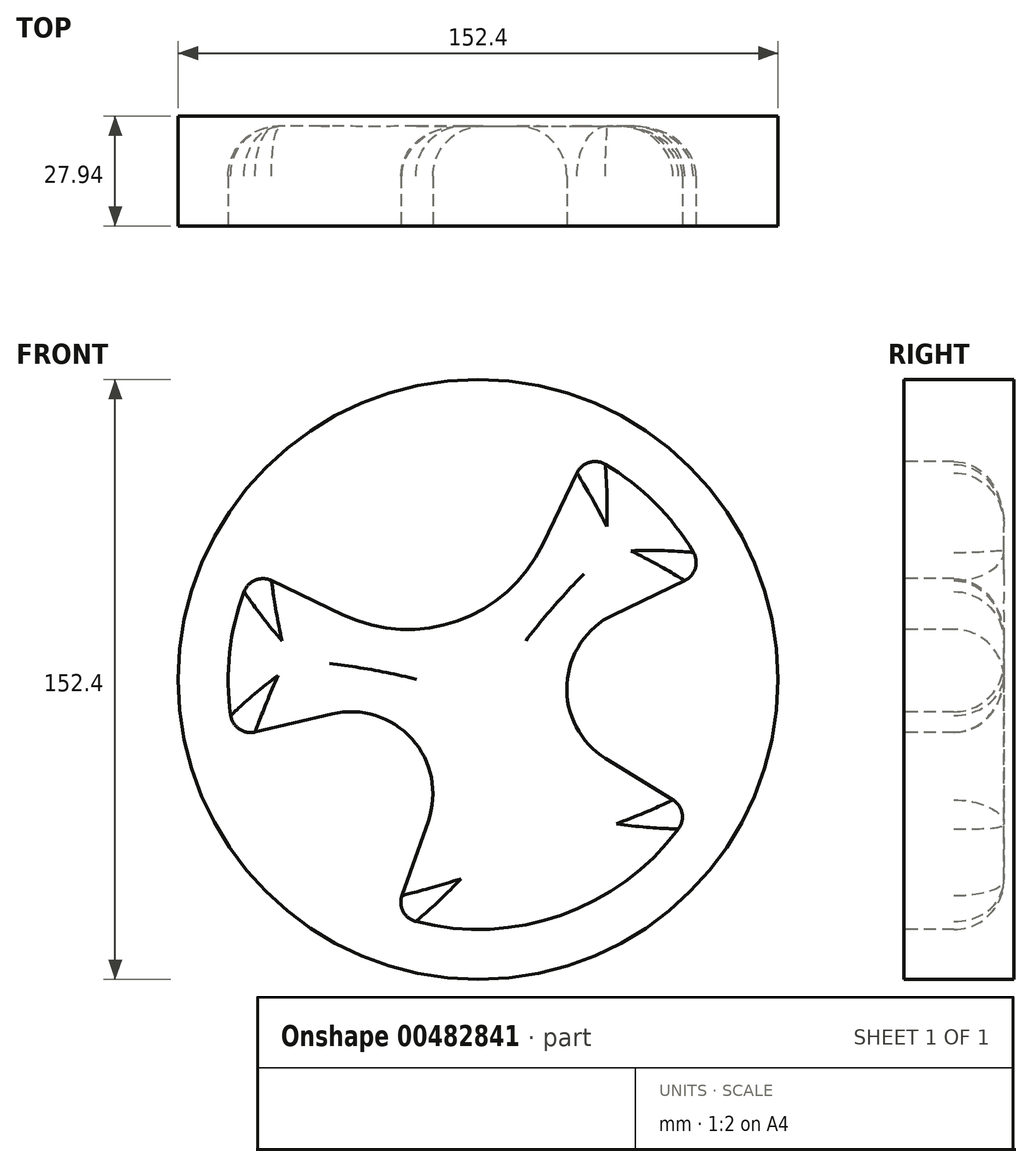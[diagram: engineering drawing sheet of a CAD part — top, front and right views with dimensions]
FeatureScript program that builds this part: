
annotation { "Feature Type Name" : "Feature", "Feature Type Description" : "" }
export const myFeature = defineFeature(function(context is Context, id is Id, definition is map)
    precondition{}
    {
        {
            var Q0;
            Q0=qCreatedBy(makeId("Front.planeOp"),FACE);
            var sketch = newSketch(context, id + "F0", { "sketchPlane" : qUnion([Q0])});
            skCircle(sketch, "E0", {"center": v(0, 0) * mm, "radius": 76.2 * mm});
            skSolve(sketch);
        }
        {
            var Q0;
            Q0=makeQuery(id+"F0.imprint","IMPRINT",FACE,{"disambiguationData":[TD([[makeQuery(id+"F0.imprint","IMPRINT",EDGE,{"derivedFrom":sQuery(id+"F0.wireOp",EDGE,"E0")}),1.0]])]});
            extrude(context, id + "F1", {"entities" : qUnion([Q0]), "depth" : 27.94 * mm});
        }
        {
            var Q0;
            Q0=makeQuery(id+"F1.opExtrude","CAP_FACE",FACE,{"disambiguationData":[OSD([sQuery(id+"F0.wireOp",EDGE,"E0")])],"isStart":false});
            var sketch = newSketch(context, id + "F2", { "sketchPlane" : qUnion([Q0])});
            skPoint(sketch, "E1.center.orphan", {"position": v(0, 50.8) * mm});
            skLineSegment(sketch, "E2.1.0", {"start": v(-34.37, 16.45) * mm, "end": v(-52.5, 25.13) * mm});
            skLineSegment(sketch, "E2.4.2", {"start": v(-12.67, -35.93) * mm, "end": v(-19.35, -54.89) * mm});
            skLineSegment(sketch, "E2.7.0", {"start": v(16.45, 34.37) * mm, "end": v(25.13, 52.5) * mm});
            skLineSegment(sketch, "E2.7.2", {"start": v(34.37, 16.45) * mm, "end": v(52.5, 25.13) * mm});
            skPoint(sketch, "E2.center", {"position": v(0, 0) * mm});
            skLineSegment(sketch, "E3", {"start": v(-37.08, -8.74) * mm, "end": v(-56.65, -13.35) * mm});
            skPoint(sketch, "E4.orphan", {"position": v(-63.84, -22.5) * mm});
            skPoint(sketch, "E5.center.orphan", {"position": v(-50.5, 5.45) * mm});
            skPoint(sketch, "E6.orphan", {"position": v(-63.84, 22.5) * mm});
            skPoint(sketch, "E7.orphan", {"position": v(-23.95, 8.45) * mm});
            skPoint(sketch, "E8.orphan", {"position": v(-23.95, -8.45) * mm});
            skLineSegment(sketch, "E9", {"start": v(32.4, -20.04) * mm, "end": v(49.5, -30.61) * mm});
            skPoint(sketch, "E10.orphan", {"position": v(22.91, -10.97) * mm});
            skPoint(sketch, "E11.orphan", {"position": v(61.06, -29.23) * mm});
            skPoint(sketch, "E12.center.orphan", {"position": v(31.86, -39.57) * mm});
            skPoint(sketch, "E13.orphan", {"position": v(8.45, -23.95) * mm});
            skPoint(sketch, "E14.orphan", {"position": v(22.5, -63.84) * mm});
            skArc(sketch, "E15", {"start": v(-59.44, 22.33) * mm, "mid": v(-63.13, 6.81) * mm, "end": v(-62.84, -9.14) * mm});
            skPoint(sketch, "E16.orphan", {"position": v(61.06, 29.23) * mm});
            skArc(sketch, "E17.trimOffspring", {"start": v(-15.83, -61.5) * mm, "mid": v(21.11, -59.89) * mm, "end": v(50.9, -37.97) * mm});
            skPoint(sketch, "E18.orphan", {"position": v(-61.06, 29.23) * mm});
            skPoint(sketch, "E19.orphan", {"position": v(-22.5, -63.84) * mm});
            skArc(sketch, "E20.trimOffspring", {"start": v(54.68, 32.3) * mm, "mid": v(44.9, 44.9) * mm, "end": v(32.3, 54.68) * mm});
            skPoint(sketch, "E21.orphan", {"position": v(22.91, 10.97) * mm});
            skArc(sketch, "E22", {"start": v(-12.67, -35.93) * mm, "mid": v(-16.81, -15.1) * mm, "end": v(-37.08, -8.74) * mm});
            skArc(sketch, "E23", {"start": v(-34.37, 16.45) * mm, "mid": v(-5.25, 14.88) * mm, "end": v(16.45, 34.37) * mm});
            skArc(sketch, "E24", {"start": v(34.37, 16.45) * mm, "mid": v(22.56, -1.21) * mm, "end": v(32.4, -20.04) * mm});
            skPoint(sketch, "E25.visualSharp", {"position": v(-57.28, 27.42) * mm});
            skArc(sketch, "E25.filletArc", {"start": v(-52.5, 25.13) * mm, "mid": v(-56.58, 25.26) * mm, "end": v(-59.44, 22.33) * mm});
            skPoint(sketch, "E26.visualSharp", {"position": v(-61.8, -14.57) * mm});
            skArc(sketch, "E26.filletArc", {"start": v(-62.84, -9.14) * mm, "mid": v(-60.67, -12.6) * mm, "end": v(-56.65, -13.35) * mm});
            skPoint(sketch, "E27.visualSharp", {"position": v(-21.11, -59.89) * mm});
            skArc(sketch, "E27.filletArc", {"start": v(-19.35, -54.89) * mm, "mid": v(-19.04, -58.97) * mm, "end": v(-15.83, -61.5) * mm});
            skPoint(sketch, "E28.visualSharp", {"position": v(54, -33.4) * mm});
            skArc(sketch, "E28.filletArc", {"start": v(50.9, -37.97) * mm, "mid": v(51.81, -33.99) * mm, "end": v(49.5, -30.61) * mm});
            skPoint(sketch, "E29.visualSharp", {"position": v(57.28, 27.42) * mm});
            skArc(sketch, "E29.filletArc", {"start": v(52.5, 25.13) * mm, "mid": v(55.16, 28.23) * mm, "end": v(54.68, 32.3) * mm});
            skPoint(sketch, "E30.visualSharp", {"position": v(27.42, 57.28) * mm});
            skArc(sketch, "E30.filletArc", {"start": v(32.3, 54.68) * mm, "mid": v(28.23, 55.16) * mm, "end": v(25.13, 52.5) * mm});
            skSolve(sketch);
        }
        {
            var Q0;
            Q0=qSketchRegion(id+"F2",true);
            extrude(context, id + "F3", {"entities" : qUnion([Q0]), "operationType" : NewBodyOperationType.REMOVE, "oppositeDirection" : true, "depth" : 25.4 * mm});
        }
        {
            var Q0;
            Q0=makeQuery(id+"F3.boolean.opBoolean","COPY",FACE,{"derivedFrom":makeQuery(id+"F3.opExtrude","CAP_FACE",FACE,{"disambiguationData":[OSD([sQuery(id+"F2.wireOp",EDGE,"E2.1.0"),sQuery(id+"F2.wireOp",EDGE,"E2.4.2"),sQuery(id+"F2.wireOp",EDGE,"E2.7.0"),sQuery(id+"F2.wireOp",EDGE,"E2.7.2"),sQuery(id+"F2.wireOp",EDGE,"E3"),sQuery(id+"F2.wireOp",EDGE,"E9"),sQuery(id+"F2.wireOp",EDGE,"E15"),sQuery(id+"F2.wireOp",EDGE,"E17.trimOffspring"),sQuery(id+"F2.wireOp",EDGE,"E20.trimOffspring"),sQuery(id+"F2.wireOp",EDGE,"E22"),sQuery(id+"F2.wireOp",EDGE,"E23"),sQuery(id+"F2.wireOp",EDGE,"E24"),sQuery(id+"F2.wireOp",EDGE,"E25.filletArc"),sQuery(id+"F2.wireOp",EDGE,"E26.filletArc"),sQuery(id+"F2.wireOp",EDGE,"E27.filletArc"),sQuery(id+"F2.wireOp",EDGE,"E28.filletArc"),sQuery(id+"F2.wireOp",EDGE,"E29.filletArc"),sQuery(id+"F2.wireOp",EDGE,"E30.filletArc")])],"isStart":false})});
            fillet(context, id + "F4", {"entities" : qUnion([Q0]), "radius" : 12.7 * mm, "tangentPropagation" : true, "allowEdgeOverflow" : false});
        }
    });
